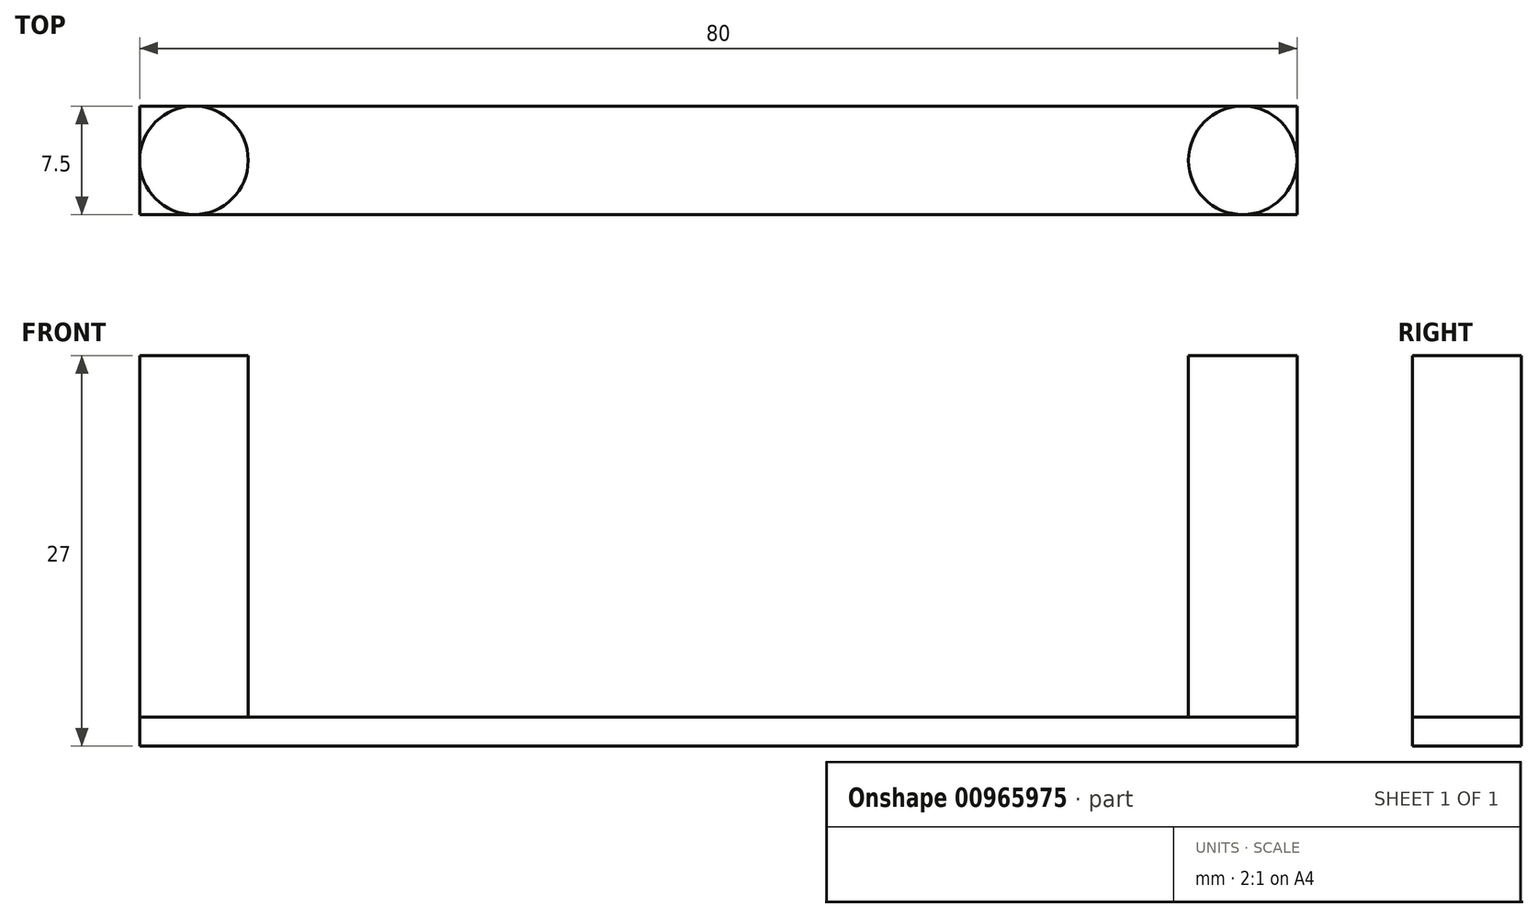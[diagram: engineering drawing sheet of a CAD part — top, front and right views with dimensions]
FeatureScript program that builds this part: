
annotation { "Feature Type Name" : "Feature", "Feature Type Description" : "" }
export const myFeature = defineFeature(function(context is Context, id is Id, definition is map)
    precondition{}
    {
        {
            var Q0;
            Q0=qCreatedBy(makeId("Top.planeOp"),FACE);
            var sketch = newSketch(context, id + "F0", { "sketchPlane" : qUnion([Q0])});
            skLineSegment(sketch, "E0.bottom", {"start": v(40, -3.75) * mm, "end": v(-40, -3.75) * mm});
            skLineSegment(sketch, "E0.top", {"start": v(40, 3.75) * mm, "end": v(-40, 3.75) * mm});
            skLineSegment(sketch, "E0.left", {"start": v(40, -3.75) * mm, "end": v(40, 3.75) * mm});
            skLineSegment(sketch, "E0.right", {"start": v(-40, -3.75) * mm, "end": v(-40, 3.75) * mm});
            skPoint(sketch, "E0.middle", {"position": v(0, 0) * mm});
            skSolve(sketch);
        }
        {
            var Q0;
            Q0 = qSketchRegion(id + "F0", true);
            extrude(context, id + "F1", {"entities" : qUnion([Q0]), "depth" : 2 * mm, "offsetDistance" : 25 * mm});
        }
        {
            var Q0;
            Q0=makeQuery(id+"F1.opExtrude","CAP_FACE",FACE,{"disambiguationData":[OSD([sQuery(id+"F0.wireOp",EDGE,"E0.bottom"),sQuery(id+"F0.wireOp",EDGE,"E0.top"),sQuery(id+"F0.wireOp",EDGE,"E0.left"),sQuery(id+"F0.wireOp",EDGE,"E0.right")])],"isStart":false});
            var sketch = newSketch(context, id + "F2", { "sketchPlane" : qUnion([Q0])});
            skCircle(sketch, "E1", {"center": v(-36.25, 0) * mm, "radius": 3.75 * mm});
            skPoint(sketch, "E1.centerSnap0", {"position": v(-40, 0) * mm});
            skCircle(sketch, "E2", {"center": v(36.25, 0) * mm, "radius": 3.75 * mm});
            skPoint(sketch, "E2.centerSnap0", {"position": v(40, 0) * mm});
            skSolve(sketch);
        }
        {
            var Q0;
            Q0 = qSketchRegion(id + "F2", true);
            extrude(context, id + "F3", {"entities" : qUnion([Q0]), "operationType" : NewBodyOperationType.ADD, "depth" : 25 * mm, "offsetDistance" : 25 * mm});
        }
    });
